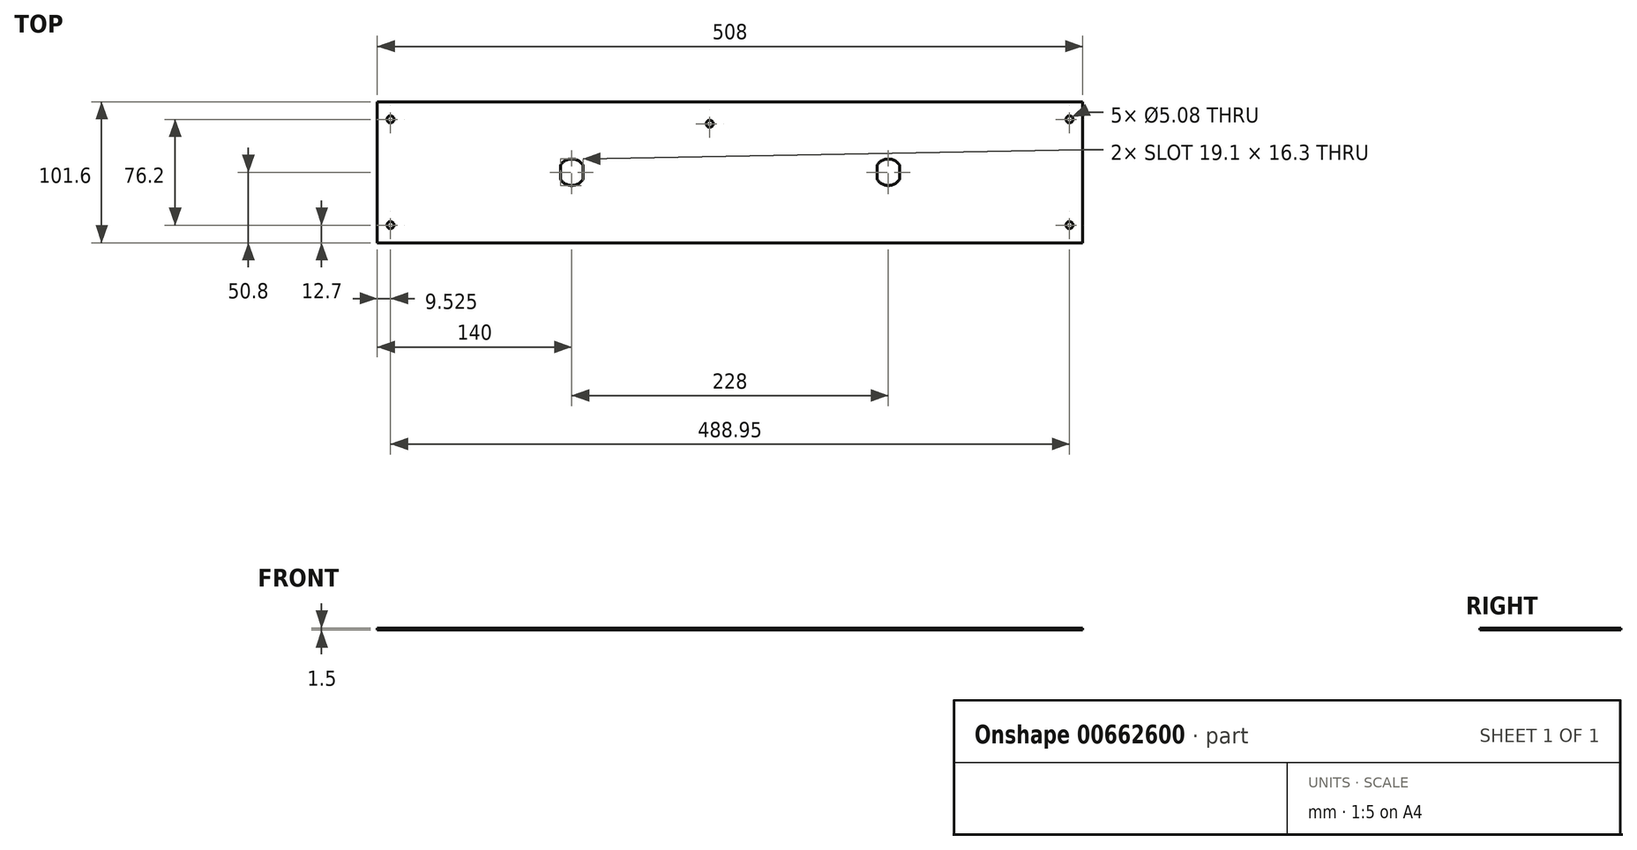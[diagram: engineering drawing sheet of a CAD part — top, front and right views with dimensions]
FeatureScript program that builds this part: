
annotation { "Feature Type Name" : "Feature", "Feature Type Description" : "" }
export const myFeature = defineFeature(function(context is Context, id is Id, definition is map)
    precondition{}
    {
        {
            var Q0;
            Q0=qCreatedBy(makeId("Top.planeOp"),FACE);
            var sketch = newSketch(context, id + "F0", { "sketchPlane" : qUnion([Q0])});
            skLineSegment(sketch, "E0.bottom", {"start": v(0, 0) * mm, "end": v(508, 0) * mm});
            skLineSegment(sketch, "E0.top", {"start": v(0, 101.6) * mm, "end": v(508, 101.6) * mm});
            skLineSegment(sketch, "E0.left", {"start": v(0, 0) * mm, "end": v(0, 101.6) * mm});
            skLineSegment(sketch, "E0.right", {"start": v(508, 0) * mm, "end": v(508, 101.6) * mm});
            skCircle(sketch, "E1", {"center": v(498.48, 12.7) * mm, "radius": 2.54 * mm});
            skCircle(sketch, "E2", {"center": v(498.48, 88.9) * mm, "radius": 2.54 * mm});
            skCircle(sketch, "E3", {"center": v(9.52, 12.7) * mm, "radius": 2.54 * mm});
            skCircle(sketch, "E4", {"center": v(9.52, 88.9) * mm, "radius": 2.54 * mm});
            skCircle(sketch, "E5", {"center": v(239.4, 85.72) * mm, "radius": 2.54 * mm});
            skSolve(sketch);
        }
        {
            var Q0;
            Q0=makeQuery(id+"F0.imprint","IMPRINT",FACE,{"disambiguationData":[TD([[makeQuery(id+"F0.imprint","IMPRINT",EDGE,{"derivedFrom":sQuery(id+"F0.wireOp",EDGE,"E0.bottom")}),1.0]])]});
            extrude(context, id + "F1", {"entities" : qUnion([Q0]), "oppositeDirection" : true, "depth" : 1.5 * mm, "offsetDistance" : 25 * mm});
        }
        {
            var Q0;
            Q0=qCreatedBy(makeId("Top.planeOp"),FACE);
            var sketch = newSketch(context, id + "F2", { "sketchPlane" : qUnion([Q0])});
            skLineSegment(sketch, "E6.0", {"start": v(0, 0) * mm, "end": v(508, 0) * mm, "construction": true});
            skLineSegment(sketch, "E6.1", {"start": v(0, 0) * mm, "end": v(0, 101.6) * mm, "construction": true});
            skArc(sketch, "E7", {"start": v(148.15, 55.78) * mm, "mid": v(140, 60.35) * mm, "end": v(131.85, 55.78) * mm});
            skLineSegment(sketch, "E8", {"start": v(131.85, 55.78) * mm, "end": v(131.85, 45.82) * mm});
            skLineSegment(sketch, "E9", {"start": v(148.15, 55.78) * mm, "end": v(148.15, 45.82) * mm});
            skArc(sketch, "E10.trimOffspring", {"start": v(131.85, 45.82) * mm, "mid": v(140, 41.25) * mm, "end": v(148.15, 45.82) * mm});
            skArc(sketch, "E11.1.0.0", {"start": v(376.15, 55.78) * mm, "mid": v(368, 60.35) * mm, "end": v(359.85, 55.78) * mm});
            skLineSegment(sketch, "E11.1.0.1", {"start": v(376.15, 55.78) * mm, "end": v(376.15, 45.82) * mm});
            skArc(sketch, "E11.1.0.2", {"start": v(359.85, 45.82) * mm, "mid": v(368, 41.25) * mm, "end": v(376.15, 45.82) * mm});
            skLineSegment(sketch, "E11.1.0.3", {"start": v(359.85, 55.78) * mm, "end": v(359.85, 45.82) * mm});
            skLineSegment(sketch, "E11.direction1", {"start": v(131.85, 55.78) * mm, "end": v(359.85, 55.78) * mm, "construction": true});
            skSolve(sketch);
        }
        {
            var Q0;
            Q0 = qSketchRegion(id + "F2", true);
            extrude(context, id + "F3", {"entities" : qUnion([Q0]), "operationType" : NewBodyOperationType.REMOVE, "oppositeDirection" : true, "depth" : 25 * mm, "offsetDistance" : 25 * mm});
        }
    });
